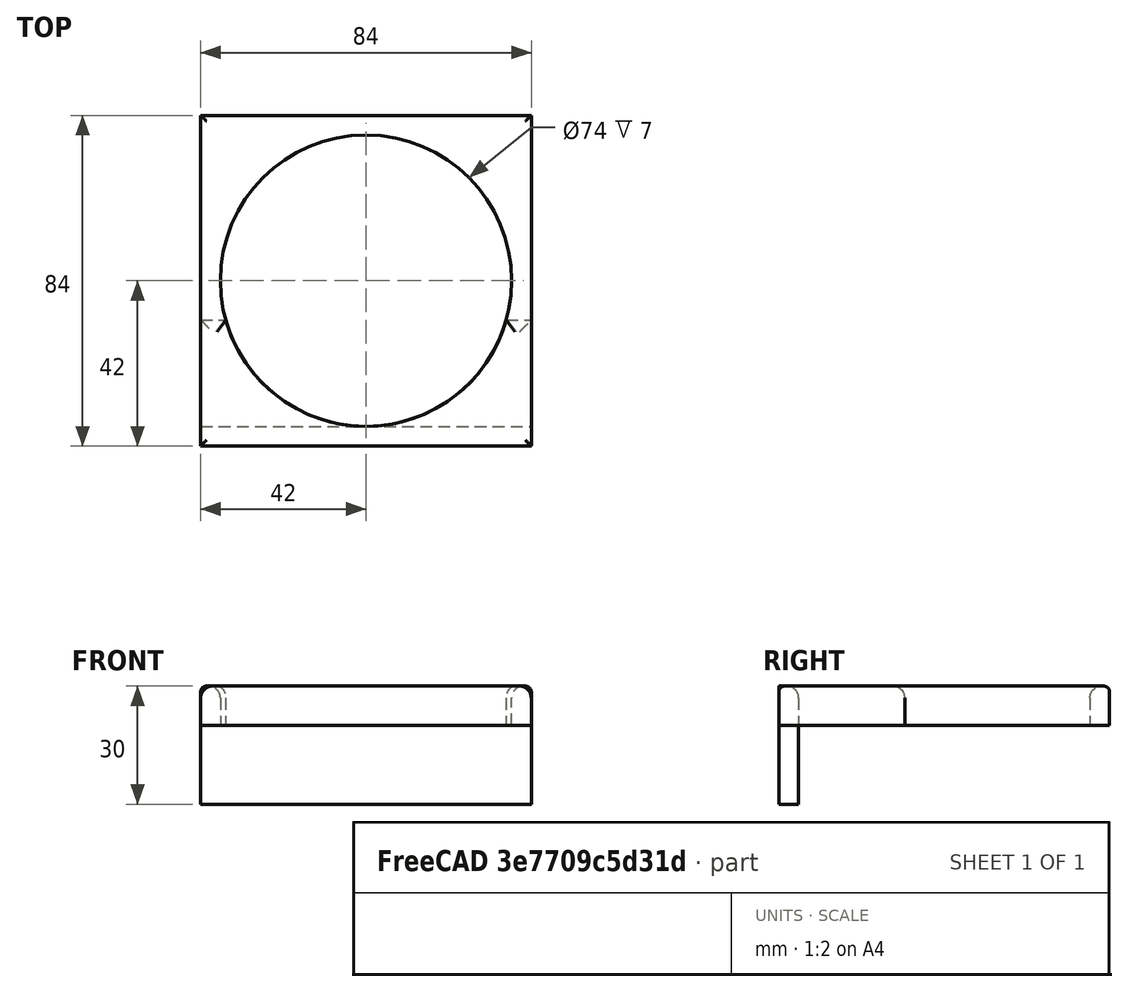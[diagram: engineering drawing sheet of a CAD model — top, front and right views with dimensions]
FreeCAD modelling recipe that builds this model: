
FCSTD DOCUMENT  (FreeCAD 0.21R33771 (Git))
Label: bar-rack-bottle-holders
License: All rights reserved
LicenseURL: http://en.wikipedia.org/wiki/All_rights_reserved
objects: Part::Box×4, Part::Cut×3, Part::Fillet×3, Part::Cylinder×2, Part::MultiFuse×1
note: 13 computed .brp shape members not serialized (recipe doc carries the construction recipe); baked Part::Feature solids carry a one-line shape summary decoded from their .brp

FEATURE [Part::Box] Box  label="Cube"
  AttacherType = Attacher::AttachEngine3D
  Height = 10
  Length = 84
  Width = 84
FEATURE [Part::Cylinder] Cylinder
  Angle = 360
  AttacherType = Attacher::AttachEngine3D
  FirstAngle = 0
  Height = 10
  Placement = pos=(42,42,0) rot=(0,0,1;0rad)
  Radius = 37
  SecondAngle = 0
FEATURE [Part::Cut] Cut
  Base = -> Box
  Tool = -> Cylinder
FEATURE [Part::Fillet] Fillet
  Base = -> Cut
  Edges = 1 edges r=3: [Edge10]
FEATURE [Part::Fillet] Fillet001  label="bar-rack-bottle-holder"
  Base = -> Fillet
  Edges = 4 edges r=1.5: [Edge2,Edge3,Edge4,Edge5]
FEATURE [Part::Box] Box001  label="Cube001"
  AttacherType = Attacher::AttachEngine3D
  Height = 10
  Length = 84
  Width = 84
FEATURE [Part::Cylinder] Cylinder001
  Angle = 360
  AttacherType = Attacher::AttachEngine3D
  FirstAngle = 0
  Height = 10
  Placement = pos=(42,42,0) rot=(0,0,1;0rad)
  Radius = 37
  SecondAngle = 0
FEATURE [Part::Cut] Cut001
  Base = -> Box001
  Tool = -> Cylinder001
FEATURE [Part::Box] Box002  label="Cube002"
  AttacherType = Attacher::AttachEngine3D
  Height = 20
  Length = 84
  Placement = pos=(0,0,-20) rot=(0,0,1;0rad)
  Width = 5
FEATURE [Part::Box] Box003  label="Cube003"
  AttacherType = Attacher::AttachEngine3D
  Height = 10
  Length = 84
  Placement = pos=(0,32,0) rot=(0,0,1;0rad)
  Width = 100
FEATURE [Part::Cut] Cut002
  Base = -> Cut001
  Tool = -> Box003
FEATURE [Part::Fillet] Fillet002
  Base = -> Cut002
  Edges = 5 edges r=3: [Edge1,Edge5,Edge6,Edge7,Edge8]
FEATURE [Part::MultiFuse] Fusion  label="bar-rack-bottle-holder-partial"
  Shapes = -> [Box002,Fillet002]
